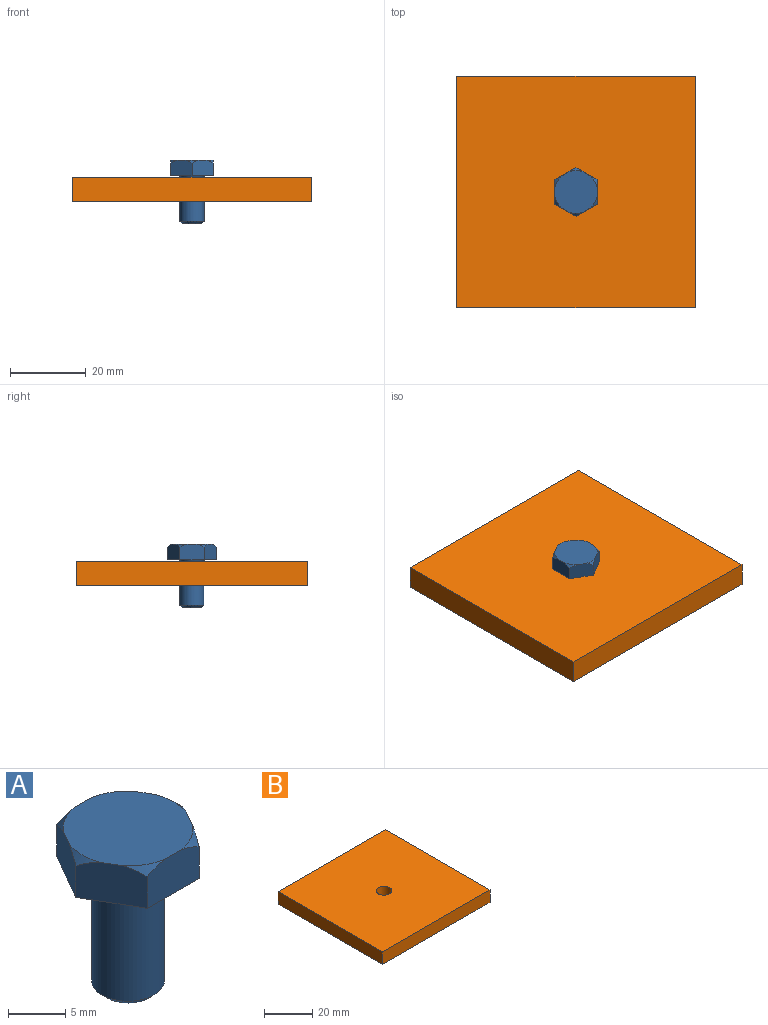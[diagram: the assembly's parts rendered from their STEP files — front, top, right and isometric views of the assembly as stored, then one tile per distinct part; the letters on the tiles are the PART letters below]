
ASSEMBLY  parts=2 mates=1
PART A: 18 faces, bbox 12.9x12.6x16.8 mm
  f0: plane 5.08x5.08mm, normal (0,0,-1), area 20.3mm2, adj f17
  f1: cylinder r=3.17mm len=11.75mm, axis (0,0,-1), area 234.4mm2, adj f16,f17
  f2: plane 12.85x11.13mm, normal (0,0,-1), area 68.9mm2, adj f3,f4,f5,f6,f7,f8,f16
  f3: plane 5.57x4.14mm, normal (0.87,0.5,0), area 25.2mm2, adj f2,f4,f6,f9,f13,f15
  f4: plane 6.43x4.14mm, normal (0,1,0), area 25.2mm2, adj f2,f3,f5,f9,f14,f15
  f5: plane 5.57x4.14mm, normal (-0.87,0.5,0), area 25.2mm2, adj f2,f4,f7,f9,f12,f14
  f6: plane 5.57x4.14mm, normal (0.87,-0.5,0), area 25.2mm2, adj f2,f3,f8,f9,f11,f13
  f7: plane 5.57x4.14mm, normal (-0.87,-0.5,0), area 25.2mm2, adj f2,f5,f8,f9,f10,f12
  f8: plane 6.43x4.14mm, normal (0,-1,0), area 25.2mm2, adj f2,f6,f7,f9,f10,f11
  f9: plane 11.32x11.13mm, normal (0,0,1), area 99.9mm2, adj f3,f4,f5,f6,f7,f8,f10,f11
  f10: cone r=5.66mm half-angle=45deg, axis (0,0,-1), area 1.7mm2, adj f7,f8,f9
  f11: cone r=5.66mm half-angle=45deg, axis (0,0,-1), area 1.7mm2, adj f6,f8,f9
  f12: cone r=5.66mm half-angle=45deg, axis (0,0,-1), area 1.7mm2, adj f5,f7,f9
  f13: cone r=5.66mm half-angle=45deg, axis (0,0,-1), area 1.7mm2, adj f3,f6,f9
  f14: cone r=5.66mm half-angle=45deg, axis (0,0,-1), area 1.7mm2, adj f4,f5,f9
  f15: cone r=5.66mm half-angle=45deg, axis (0,0,-1), area 1.7mm2, adj f3,f4,f9
  f16: torus R=3.49mm, axis (0,0,1), area 10.3mm2, adj f1,f2
  f17: cone r=2.54mm half-angle=45deg, axis (0,0,1), area 16.1mm2, adj f0,f1
PART B: 7 faces, bbox 63x61.1x6.4 mm
  f0: plane 61.14x6.35mm, normal (1,0,0), area 388.2mm2, adj f1,f4,f5,f6
  f1: plane 62.96x6.35mm, normal (0,1,0), area 399.8mm2, adj f0,f2,f5,f6
  f2: plane 61.14x6.35mm, normal (-1,0,0), area 388.2mm2, adj f1,f4,f5,f6
  f3: cylinder r=3.17mm len=6.35mm, axis (0,0,1), area 126.7mm2, adj f5,f6
  f4: plane 62.96x6.35mm, normal (0,-1,0), area 399.8mm2, adj f0,f2,f5,f6
  f5: plane 62.96x61.14mm, normal (0,0,-1), area 3817.4mm2, adj f0,f1,f2,f3,f4
  f6: plane 62.96x61.14mm, normal (0,0,1), area 3817.4mm2, adj f0,f1,f2,f3,f4
PLACE A rot(axis=(0,0,1),90deg) t=(-3.09,3.48,-28.79)mm
PLACE B t=(-3.09,3.48,-3.71)mm fixed
MATE slider A.f1 <-> B.f3  axis (0,0,-1) through (-3.09,3.48,-3.71)mm
